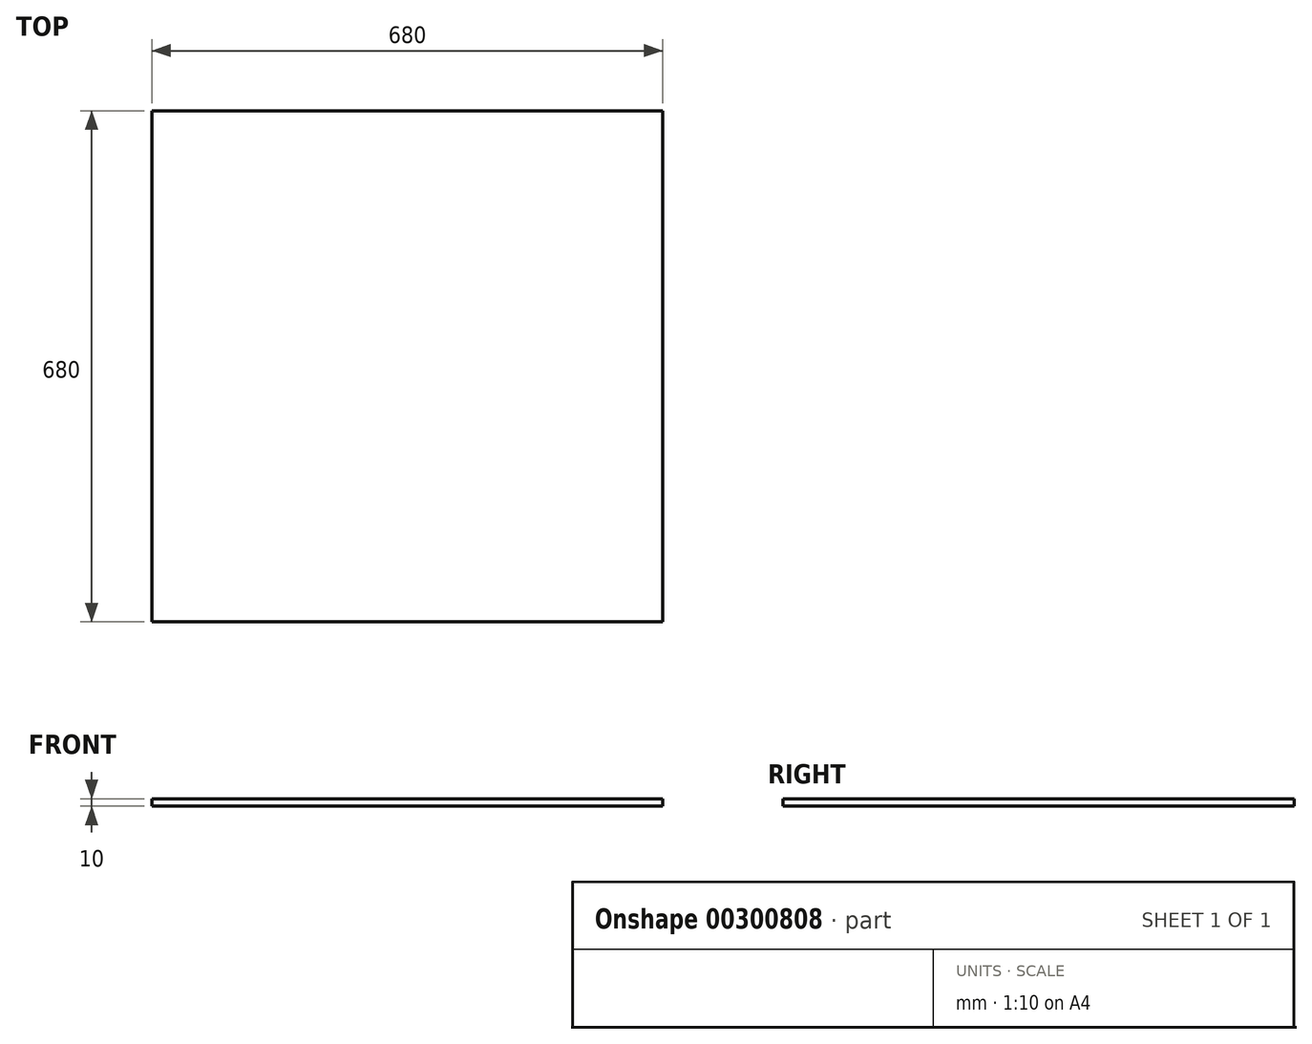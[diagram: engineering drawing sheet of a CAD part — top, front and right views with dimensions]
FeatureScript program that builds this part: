
annotation { "Feature Type Name" : "Feature", "Feature Type Description" : "" }
export const myFeature = defineFeature(function(context is Context, id is Id, definition is map)
    precondition{}
    {
        {
            var Q0;
            Q0=qCreatedBy(makeId("Front.planeOp"),FACE);
            var sketch = newSketch(context, id + "F0", { "sketchPlane" : qUnion([Q0])});
            skLineSegment(sketch, "E0.bottom", {"start": v(-340.86, -144.66) * mm, "end": v(339.14, -144.66) * mm});
            skLineSegment(sketch, "E0.top", {"start": v(-340.86, -154.66) * mm, "end": v(339.14, -154.66) * mm});
            skLineSegment(sketch, "E0.left", {"start": v(-340.86, -144.66) * mm, "end": v(-340.86, -154.66) * mm});
            skLineSegment(sketch, "E0.right", {"start": v(339.14, -144.66) * mm, "end": v(339.14, -154.66) * mm});
            skSolve(sketch);
        }
        {
            var Q0;
            Q0 = qSketchRegion(id + "F0", true);
            extrude(context, id + "F1", {"entities" : qUnion([Q0]), "depth" : 680 * mm});
        }
    });
